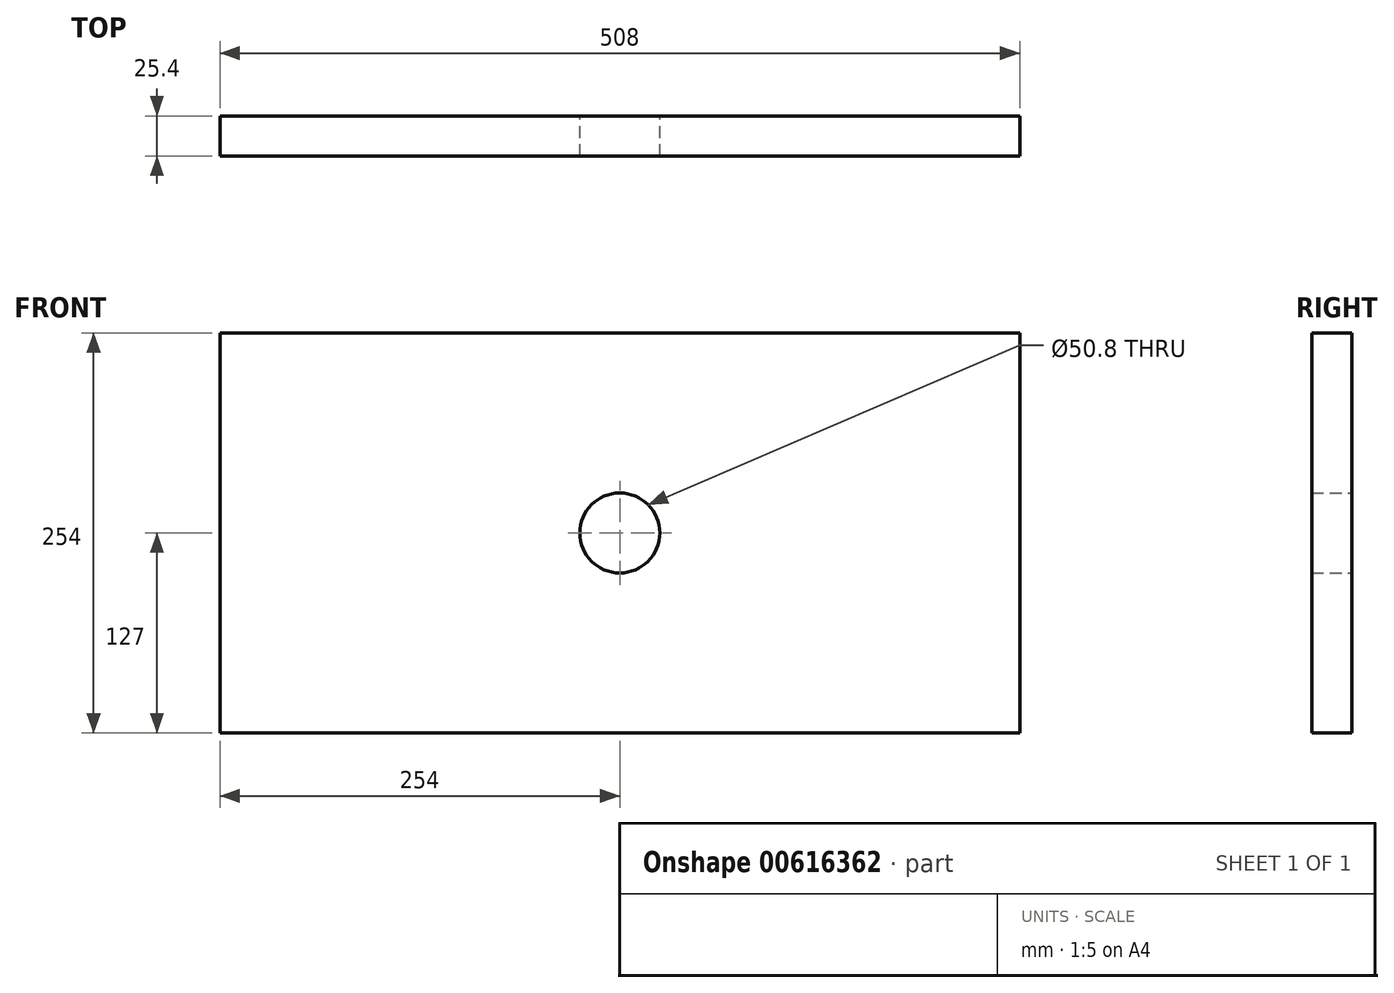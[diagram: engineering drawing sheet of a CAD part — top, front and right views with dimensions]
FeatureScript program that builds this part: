
annotation { "Feature Type Name" : "Feature", "Feature Type Description" : "" }
export const myFeature = defineFeature(function(context is Context, id is Id, definition is map)
    precondition{}
    {
        {
            var Q0;
            Q0=qCreatedBy(makeId("Front.planeOp"),FACE);
            var sketch = newSketch(context, id + "F0", { "sketchPlane" : qUnion([Q0])});
            skLineSegment(sketch, "E0.bottom", {"start": v(-254, 254) * mm, "end": v(254, 254) * mm});
            skLineSegment(sketch, "E0.top", {"start": v(-254, 0) * mm, "end": v(254, 0) * mm});
            skLineSegment(sketch, "E0.left", {"start": v(-254, 254) * mm, "end": v(-254, 0) * mm});
            skLineSegment(sketch, "E0.right", {"start": v(254, 254) * mm, "end": v(254, 0) * mm});
            skCircle(sketch, "E1", {"center": v(0, 127) * mm, "radius": 25.4 * mm});
            skSolve(sketch);
        }
        {
            var Q0;
            Q0 = qSketchRegion(id + "F0", true);
            extrude(context, id + "F1", {"entities" : qUnion([Q0]), "depth" : 25.4 * mm, "offsetDistance" : 25.4 * mm});
        }
    });
